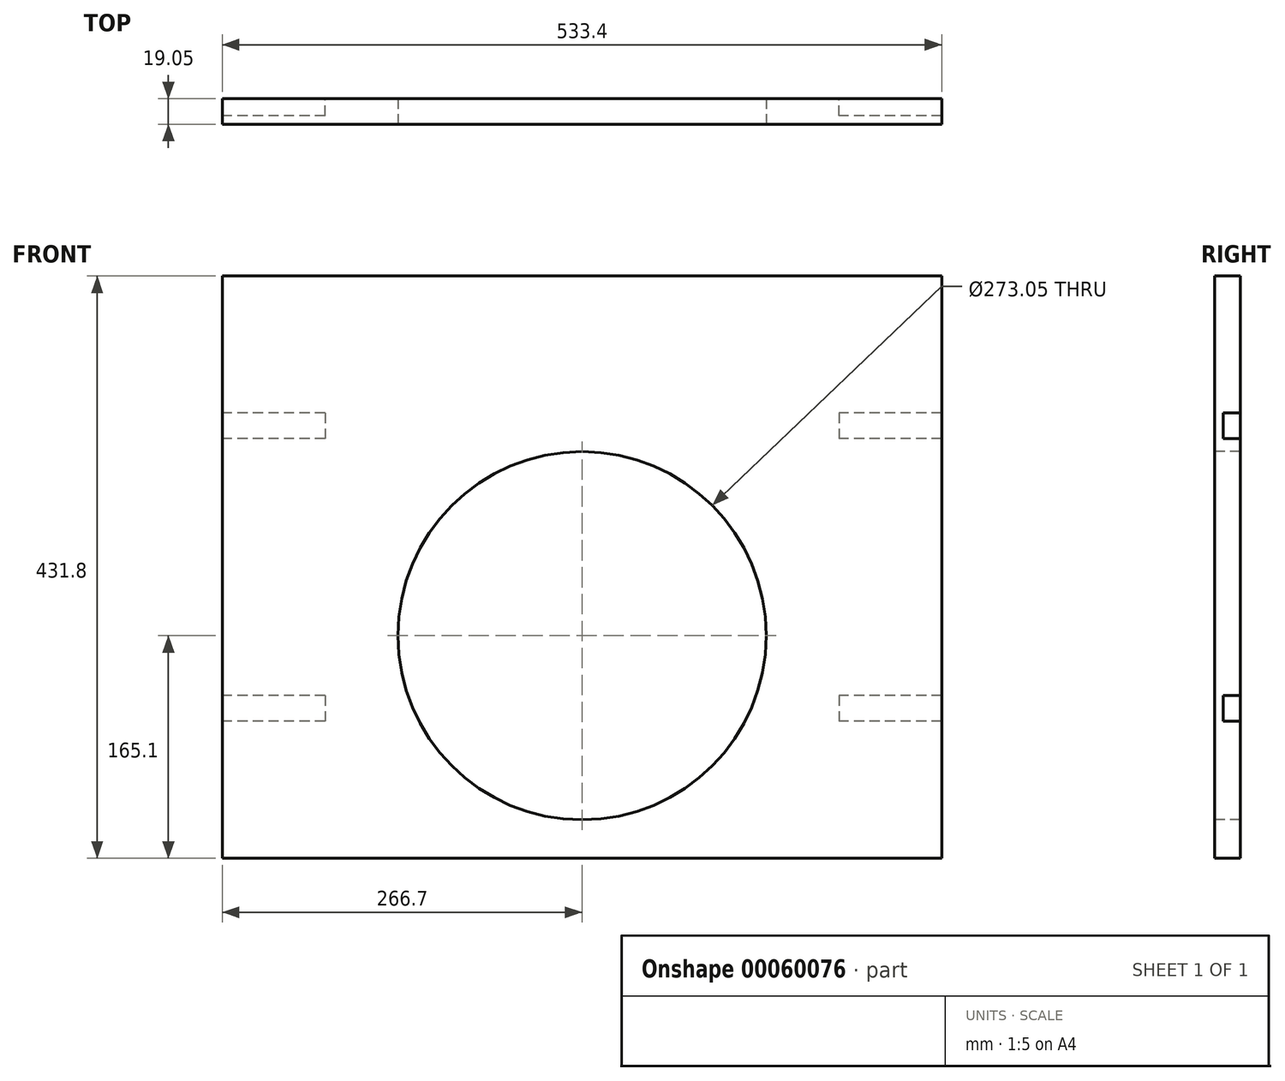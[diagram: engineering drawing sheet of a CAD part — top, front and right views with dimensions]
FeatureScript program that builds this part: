
annotation { "Feature Type Name" : "Feature", "Feature Type Description" : "" }
export const myFeature = defineFeature(function(context is Context, id is Id, definition is map)
    precondition{}
    {
        {
            var Q0;
            Q0=qCreatedBy(makeId("Front.planeOp"),FACE);
            var sketch = newSketch(context, id + "F0", { "sketchPlane" : qUnion([Q0])});
            skLineSegment(sketch, "E0.bottom", {"start": v(-266.7, -215.9) * mm, "end": v(266.7, -215.9) * mm});
            skLineSegment(sketch, "E0.top", {"start": v(-266.7, 215.9) * mm, "end": v(266.7, 215.9) * mm});
            skLineSegment(sketch, "E0.left", {"start": v(-266.7, -215.9) * mm, "end": v(-266.7, 215.9) * mm});
            skLineSegment(sketch, "E0.right", {"start": v(266.7, -215.9) * mm, "end": v(266.7, 215.9) * mm});
            skLineSegment(sketch, "E1", {"start": v(-266.7, 215.9) * mm, "end": v(266.7, -215.9) * mm, "construction": true});
            skCircle(sketch, "E2", {"center": v(0, -50.8) * mm, "radius": 136.53 * mm});
            skSolve(sketch);
        }
        {
            var Q0;
            Q0 = qSketchRegion(id + "F0", true);
            extrude(context, id + "F1", {"entities" : qUnion([Q0]), "oppositeDirection" : true, "depth" : 19.05 * mm});
        }
        {
            var Q0;
            Q0=makeQuery(id+"F1.opExtrude","CAP_FACE",FACE,{"disambiguationData":[OSD([sQuery(id+"F0.wireOp",EDGE,"E0.bottom"),sQuery(id+"F0.wireOp",EDGE,"E0.top"),sQuery(id+"F0.wireOp",EDGE,"E0.left"),sQuery(id+"F0.wireOp",EDGE,"E0.right"),sQuery(id+"F0.wireOp",EDGE,"E2")])],"isStart":false});
            var sketch = newSketch(context, id + "F3", { "sketchPlane" : qUnion([Q0])});
            skLineSegment(sketch, "E3.bottom", {"start": v(-266.7, 114.3) * mm, "end": v(-190.5, 114.3) * mm});
            skLineSegment(sketch, "E3.top", {"start": v(-266.7, 95.25) * mm, "end": v(-190.5, 95.25) * mm});
            skLineSegment(sketch, "E3.left", {"start": v(-266.7, 114.3) * mm, "end": v(-266.7, 95.25) * mm});
            skLineSegment(sketch, "E3.right", {"start": v(-190.5, 114.3) * mm, "end": v(-190.5, 95.25) * mm});
            skLineSegment(sketch, "E4.bottom", {"start": v(-266.7, -95.25) * mm, "end": v(-190.5, -95.25) * mm});
            skLineSegment(sketch, "E4.top", {"start": v(-266.7, -114.3) * mm, "end": v(-190.5, -114.3) * mm});
            skLineSegment(sketch, "E4.left", {"start": v(-266.7, -95.25) * mm, "end": v(-266.7, -114.3) * mm});
            skLineSegment(sketch, "E4.right", {"start": v(-190.5, -95.25) * mm, "end": v(-190.5, -114.3) * mm});
            skLineSegment(sketch, "E5.bottom", {"start": v(190.5, 114.3) * mm, "end": v(266.7, 114.3) * mm});
            skLineSegment(sketch, "E5.top", {"start": v(190.5, 95.25) * mm, "end": v(266.7, 95.25) * mm});
            skLineSegment(sketch, "E5.left", {"start": v(190.5, 114.3) * mm, "end": v(190.5, 95.25) * mm});
            skLineSegment(sketch, "E5.right", {"start": v(266.7, 114.3) * mm, "end": v(266.7, 95.25) * mm});
            skLineSegment(sketch, "E6.bottom", {"start": v(190.5, -95.25) * mm, "end": v(266.7, -95.25) * mm});
            skLineSegment(sketch, "E6.top", {"start": v(190.5, -114.3) * mm, "end": v(266.7, -114.3) * mm});
            skLineSegment(sketch, "E6.left", {"start": v(190.5, -95.25) * mm, "end": v(190.5, -114.3) * mm});
            skLineSegment(sketch, "E6.right", {"start": v(266.7, -95.25) * mm, "end": v(266.7, -114.3) * mm});
            skSolve(sketch);
        }
        {
            var Q0;
            Q0 = qSketchRegion(id + "F3", true);
            extrude(context, id + "F4", {"entities" : qUnion([Q0]), "operationType" : NewBodyOperationType.REMOVE, "oppositeDirection" : true, "depth" : 12.7 * mm});
        }
    });
